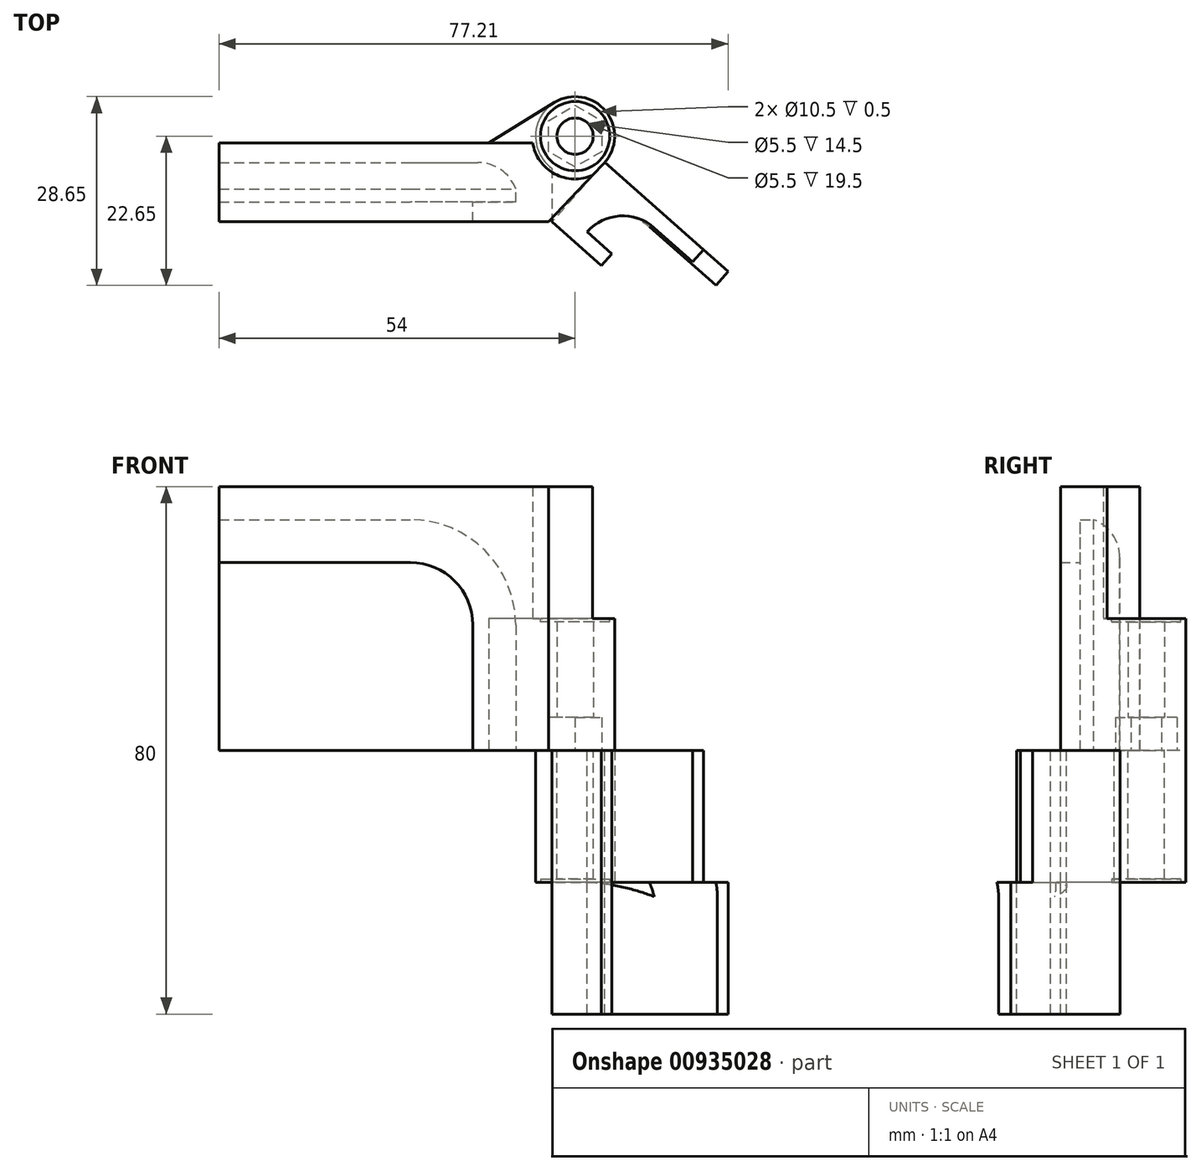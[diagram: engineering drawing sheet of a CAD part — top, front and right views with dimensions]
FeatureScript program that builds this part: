
annotation { "Feature Type Name" : "Feature", "Feature Type Description" : "" }
export const myFeature = defineFeature(function(context is Context, id is Id, definition is map)
    precondition{}
    {
        {
            var Q0;
            Q0=qCreatedBy(makeId("Front.planeOp"),FACE);
            var sketch = newSketch(context, id + "F0", { "sketchPlane" : qUnion([Q0])});
            skLineSegment(sketch, "E0.bottom", {"start": v(0, 0) * mm, "end": v(45, 0) * mm});
            skLineSegment(sketch, "E0.top", {"start": v(0, 35) * mm, "end": v(29, 35) * mm});
            skLineSegment(sketch, "E0.left", {"start": v(0, 0) * mm, "end": v(0, 35) * mm});
            skLineSegment(sketch, "E0.right", {"start": v(45, 0) * mm, "end": v(45, 19) * mm});
            skLineSegment(sketch, "E1.bottom", {"start": v(0, 0) * mm, "end": v(50, 0) * mm});
            skLineSegment(sketch, "E1.top", {"start": v(0, 40) * mm, "end": v(50, 40) * mm});
            skLineSegment(sketch, "E1.left", {"start": v(0, 0) * mm, "end": v(0, 40) * mm});
            skLineSegment(sketch, "E1.right", {"start": v(50, 0) * mm, "end": v(50, 40) * mm});
            skPoint(sketch, "E2.visualSharp", {"position": v(45, 35) * mm});
            skArc(sketch, "E2.filletArc", {"start": v(45, 19) * mm, "mid": v(40.31, 30.31) * mm, "end": v(29, 35) * mm});
            skSolve(sketch);
        }
        {
            var Q0;
            {var subQ4=sQuery(id+"F0.wireOp",EDGE,"E0.top");Q0=makeQuery(id+"F0.imprint","IMPRINT",FACE,{"disambiguationData":[TD([[makeQuery(id+"F0.imprint","IMPRINT",EDGE,{"derivedFrom":subQ4}),1.0]])]});}
            extrude(context, id + "F1", {"entities" : qUnion([Q0]), "depth" : 6 * mm, "offsetDistance" : 25 * mm});
        }
        {
            var Q0;
            {var subQ4=sQuery(id+"F0.wireOp",EDGE,"E0.top");Q0=makeQuery(id+"F0.imprint","IMPRINT",FACE,{"disambiguationData":[TD([[makeQuery(id+"F0.imprint","IMPRINT",EDGE,{"derivedFrom":subQ4}),-1.0]])]});}
            var Q1;
            {var subQ4=sQuery(id+"F0.wireOp",EDGE,"E0.top");Q1=makeQuery(id+"F0.imprint","IMPRINT",FACE,{"disambiguationData":[TD([[makeQuery(id+"F0.imprint","IMPRINT",EDGE,{"derivedFrom":subQ4}),1.0]])]});}
            extrude(context, id + "F2", {"entities" : qUnion([Q0, Q1]), "operationType" : NewBodyOperationType.ADD, "oppositeDirection" : true, "depth" : 3 * mm, "offsetDistance" : 25 * mm});
        }
        {
            var Q0;
            Q0=qCreatedBy(makeId("Right.planeOp"),FACE);
            var sketch = newSketch(context, id + "F3", { "sketchPlane" : qUnion([Q0])});
            skArc(sketch, "E3", {"start": v(0, 29.25) * mm, "mid": v(-1.1, 32.76) * mm, "end": v(-4.01, 35) * mm});
            skPoint(sketch, "E4.orphan", {"position": v(0, 35) * mm});
            skLineSegment(sketch, "E5", {"start": v(0, 29.25) * mm, "end": v(0, 35) * mm});
            skLineSegment(sketch, "E6", {"start": v(0, 35) * mm, "end": v(-4.01, 35) * mm});
            skPoint(sketch, "E7.0.start.orphan", {"position": v(-6, 35) * mm});
            skSolve(sketch);
        }
        {
            var Q0;
            Q0 = qSketchRegion(id + "F3", true);
            var Q1;
            Q1=sQuery(id+"F0.wireOp",EDGE,"E0.top");
            var Q2;
            Q2=sQuery(id+"F0.wireOp",EDGE,"E2.filletArc");
            var Q3;
            Q3=sQuery(id+"F0.wireOp",EDGE,"E0.right");
            sweep(context, id + "F4", {"operationType" : NewBodyOperationType.ADD, "profiles" : qUnion([Q0]), "path" : qUnion([Q1, Q2, Q3])});
        }
        {
            var Q0;
            Q0=makeQuery(id+"F1.opExtrude","CAP_FACE",FACE,{"disambiguationData":[OSD([sQuery(id+"F0.wireOp",EDGE,"E0.top"),sQuery(id+"F0.wireOp",EDGE,"E0.right"),sQuery(id+"F0.wireOp",EDGE,"E1.bottom"),sQuery(id+"F0.wireOp",EDGE,"E1.top"),sQuery(id+"F0.wireOp",EDGE,"E1.left"),sQuery(id+"F0.wireOp",EDGE,"E1.right"),sQuery(id+"F0.wireOp",EDGE,"E2.filletArc")])],"isStart":false});
            var sketch = newSketch(context, id + "F5", { "sketchPlane" : qUnion([Q0])});
            skLineSegment(sketch, "E8.0", {"start": v(0, 40) * mm, "end": v(50, 40) * mm});
            skLineSegment(sketch, "E9.0", {"start": v(50, 0) * mm, "end": v(50, 40) * mm});
            skLineSegment(sketch, "E10", {"start": v(0, 40) * mm, "end": v(0, 33.5) * mm});
            skLineSegment(sketch, "E11.0", {"start": v(43.5, 0) * mm, "end": v(43.5, 19) * mm});
            skArc(sketch, "E11.1", {"start": v(43.5, 19) * mm, "mid": v(39.25, 29.25) * mm, "end": v(29, 33.5) * mm});
            skLineSegment(sketch, "E11.2", {"start": v(0, 33.5) * mm, "end": v(29, 33.5) * mm});
            skLineSegment(sketch, "E12", {"start": v(43.5, 0) * mm, "end": v(50, 0) * mm});
            skLineSegment(sketch, "E13.0", {"start": v(38.5, 0) * mm, "end": v(38.5, 19) * mm});
            skArc(sketch, "E13.1", {"start": v(38.5, 19) * mm, "mid": v(35.72, 25.72) * mm, "end": v(29, 28.5) * mm});
            skLineSegment(sketch, "E13.2", {"start": v(0, 28.5) * mm, "end": v(29, 28.5) * mm});
            skLineSegment(sketch, "E14", {"start": v(0, 33.5) * mm, "end": v(0, 28.5) * mm});
            skLineSegment(sketch, "E15", {"start": v(38.5, 0) * mm, "end": v(43.5, 0) * mm});
            skLineSegment(sketch, "E16", {"start": v(29, 33.5) * mm, "end": v(29, 28.5) * mm});
            skLineSegment(sketch, "E17", {"start": v(43.5, 19) * mm, "end": v(38.5, 19) * mm});
            skSolve(sketch);
        }
        {
            var Q0;
            {var subQ5=sQuery(id+"F5.wireOp",EDGE,"E8.0");Q0=makeQuery(id+"F5.imprint","IMPRINT",FACE,{"disambiguationData":[TD([[makeQuery(id+"F5.imprint","IMPRINT",EDGE,{"derivedFrom":subQ5}),-1.0]])]});}
            var Q1;
            {var subQ1=sQuery(id+"F5.wireOp",EDGE,"E11.0");Q1=makeQuery(id+"F5.imprint","IMPRINT",FACE,{"disambiguationData":[TD([[makeQuery(id+"F5.imprint","IMPRINT",EDGE,{"derivedFrom":subQ1}),-1.0]])]});}
            var Q2;
            Q2=makeQuery(id+"F5.imprint","IMPRINT",FACE,{"disambiguationData":[TD([[makeQuery(id+"F5.imprint","IMPRINT",EDGE,{"derivedFrom":sQuery(id+"F5.wireOp",EDGE,"E11.0")}),1.0]])]});
            var Q3;
            Q3=makeQuery(id+"F5.imprint","IMPRINT",FACE,{"disambiguationData":[TD([[makeQuery(id+"F5.imprint","IMPRINT",EDGE,{"derivedFrom":sQuery(id+"F5.wireOp",EDGE,"E11.2")}),-1.0]])]});
            var Q4;
            Q4=makeQuery(id+"F5.imprint","IMPRINT",FACE,{"disambiguationData":[TD([[makeQuery(id+"F5.imprint","IMPRINT",EDGE,{"derivedFrom":sQuery(id+"F5.wireOp",EDGE,"E11.1")}),1.0]])]});
            extrude(context, id + "F6", {"entities" : qUnion([Q0, Q1, Q2, Q3, Q4]), "operationType" : NewBodyOperationType.ADD, "depth" : 3 * mm, "offsetDistance" : 25 * mm});
        }
        {
            var Q0;
            Q0=qCreatedBy(makeId("Top.planeOp"),FACE);
            var sketch = newSketch(context, id + "F7", { "sketchPlane" : qUnion([Q0])});
            skCircle(sketch, "E18", {"center": v(54, 4) * mm, "radius": 6 * mm});
            skCircle(sketch, "E19", {"center": v(54, 4) * mm, "radius": 2.75 * mm});
            skCircle(sketch, "E20.cCircle", {"center": v(54, 4) * mm, "radius": 4.68 * mm, "construction": true});
            skLineSegment(sketch, "E20.0", {"start": v(58.05, 6.34) * mm, "end": v(58.05, 1.66) * mm});
            skLineSegment(sketch, "E20.1", {"start": v(58.05, 1.66) * mm, "end": v(54, -0.68) * mm});
            skLineSegment(sketch, "E20.2", {"start": v(54, -0.68) * mm, "end": v(49.95, 1.66) * mm});
            skLineSegment(sketch, "E20.3", {"start": v(49.95, 1.66) * mm, "end": v(49.95, 6.34) * mm});
            skLineSegment(sketch, "E20.4", {"start": v(49.95, 6.34) * mm, "end": v(54, 8.68) * mm});
            skLineSegment(sketch, "E20.5", {"start": v(54, 8.68) * mm, "end": v(58.05, 6.34) * mm});
            skLineSegment(sketch, "E21", {"start": v(58.37, -0.11) * mm, "end": v(50, -9) * mm});
            skPoint(sketch, "E22.0", {"position": v(50, -9) * mm});
            skPoint(sketch, "E23.0", {"position": v(50, 3) * mm});
            skLineSegment(sketch, "E24", {"start": v(50.87, 9.12) * mm, "end": v(40.87, 3) * mm});
            skLineSegment(sketch, "E25", {"start": v(40.87, 3) * mm, "end": v(48.08, 3) * mm});
            skLineSegment(sketch, "E26", {"start": v(50, -9) * mm, "end": v(50, -0.47) * mm});
            skSolve(sketch);
        }
        {
            var Q0;
            {var subQ0=sQuery(id+"F7.wireOp",EDGE,"8cb6e2d6-110c-4912-a526-4a30d62b72c0");Q0=makeQuery(id+"F7.imprint","IMPRINT",FACE,{"disambiguationData":[TD([[makeQuery(id+"F7.imprint","IMPRINT",EDGE,{"derivedFrom":subQ0}),1.0]])]});}
            var Q1;
            Q1=makeQuery(id+"F7.imprint","IMPRINT",FACE,{"disambiguationData":[TD([[makeQuery(id+"F7.imprint","IMPRINT",EDGE,{"derivedFrom":sQuery(id+"F7.wireOp",EDGE,"E20.0")}),1.0]])]});
            var Q2;
            {var subQ0=sQuery(id+"F7.wireOp",EDGE,"0a3eac35-8b06-4a45-9f79-940ba3505365");Q2=makeQuery(id+"F7.imprint","IMPRINT",FACE,{"disambiguationData":[TD([[makeQuery(id+"F7.imprint","IMPRINT",EDGE,{"derivedFrom":subQ0}),-1.0]])]});}
            var Q3;
            {var subQ0=sQuery(id+"F7.wireOp",EDGE,"E24");Q3=makeQuery(id+"F7.imprint","IMPRINT",FACE,{"disambiguationData":[TD([[makeQuery(id+"F7.imprint","IMPRINT",EDGE,{"derivedFrom":subQ0}),1.0]])]});}
            var Q4;
            {var subQ0=sQuery(id+"F7.wireOp",EDGE,"E21");Q4=makeQuery(id+"F7.imprint","IMPRINT",FACE,{"disambiguationData":[TD([[makeQuery(id+"F7.imprint","IMPRINT",EDGE,{"derivedFrom":subQ0}),-1.0]])]});}
            extrude(context, id + "F8", {"entities" : qUnion([Q0, Q1, Q2, Q3, Q4]), "operationType" : NewBodyOperationType.ADD, "depth" : 5 * mm, "offsetDistance" : 25 * mm});
        }
        {
            var Q0;
            Q0=makeQuery(id+"F7.imprint","IMPRINT",FACE,{"disambiguationData":[TD([[makeQuery(id+"F7.imprint","IMPRINT",EDGE,{"derivedFrom":sQuery(id+"F7.wireOp",EDGE,"E19")}),-1.0]])]});
            extrude(context, id + "F9", {"entities" : qUnion([Q0]), "operationType" : NewBodyOperationType.REMOVE, "depth" : 5 * mm, "offsetDistance" : 25 * mm});
        }
        {
            var Q0;
            Q0=makeQuery(id+"F8.opExtrude","CAP_FACE",FACE,{"disambiguationData":[OSD([sQuery(id+"F7.wireOp",EDGE,"E18"),sQuery(id+"F7.wireOp",EDGE,"8cb6e2d6-110c-4912-a526-4a30d62b72c0"),sQuery(id+"F7.wireOp",EDGE,"0a3eac35-8b06-4a45-9f79-940ba3505365"),sQuery(id+"F7.wireOp",EDGE,"E20.0"),sQuery(id+"F7.wireOp",EDGE,"E20.1"),sQuery(id+"F7.wireOp",EDGE,"E20.2"),sQuery(id+"F7.wireOp",EDGE,"E20.3"),sQuery(id+"F7.wireOp",EDGE,"E20.4"),sQuery(id+"F7.wireOp",EDGE,"E20.5"),sQuery(id+"F7.wireOp",EDGE,"4abc8ff2-313a-444c-833f-485fd2e250e1.0")])],"isStart":false});
            var sketch = newSketch(context, id + "F10", { "sketchPlane" : qUnion([Q0])});
            skCircle(sketch, "E27.0", {"center": v(54, 4) * mm, "radius": 2.75 * mm});
            skCircle(sketch, "E28.0", {"center": v(54, 4) * mm, "radius": 6 * mm});
            skLineSegment(sketch, "E29.0", {"start": v(58.37, -0.11) * mm, "end": v(50, -9) * mm});
            skLineSegment(sketch, "E30.0", {"start": v(50, -9) * mm, "end": v(50, -0.47) * mm});
            skArc(sketch, "E31.0.0", {"start": v(58.37, -0.11) * mm, "mid": v(58.66, 7.78) * mm, "end": v(50.87, 9.12) * mm});
            skArc(sketch, "E31.0.1", {"start": v(50.87, 9.12) * mm, "mid": v(48.54, 6.49) * mm, "end": v(48.08, 3) * mm});
            skArc(sketch, "E31.0.2", {"start": v(48.08, 3) * mm, "mid": v(48.75, 1.1) * mm, "end": v(50, -0.47) * mm});
            skArc(sketch, "E31.0.3", {"start": v(50, -0.47) * mm, "mid": v(54.26, -2) * mm, "end": v(58.37, -0.11) * mm});
            skArc(sketch, "E32.0.0", {"start": v(48.08, 3) * mm, "mid": v(48.54, 6.49) * mm, "end": v(50.87, 9.12) * mm});
            skLineSegment(sketch, "E32.0.1", {"start": v(50.87, 9.12) * mm, "end": v(40.87, 3) * mm});
            skLineSegment(sketch, "E32.0.2", {"start": v(40.87, 3) * mm, "end": v(48.08, 3) * mm});
            skArc(sketch, "E33.0.0", {"start": v(58.37, -0.11) * mm, "mid": v(54.26, -2) * mm, "end": v(50, -0.47) * mm});
            skLineSegment(sketch, "E33.0.1", {"start": v(50, -0.47) * mm, "end": v(50, -9) * mm});
            skLineSegment(sketch, "E33.0.2", {"start": v(50, -9) * mm, "end": v(58.37, -0.11) * mm});
            skSolve(sketch);
        }
        {
            var Q0;
            {var subQ2=sQuery(id+"F10.wireOp",EDGE,"E33.0.1");Q0=makeQuery(id+"F10.imprint","IMPRINT",FACE,{"disambiguationData":[TD([[makeQuery(id+"F10.imprint","IMPRINT",EDGE,{"derivedFrom":subQ2}),-1.0]])]});}
            var Q1;
            {var subQ8=sQuery(id+"F7.wireOp",EDGE,"E20.0");Q1=makeQuery(id+"F10.imprint","IMPRINT",FACE,{"disambiguationData":[TD([[makeQuery(id+"F10.imprint","IMPRINT",EDGE,{"derivedFrom":makeQuery(id+"F8.opExtrude","CAP_EDGE",EDGE,{"disambiguationData":[OSD([subQ8])],"isStart":false})}),1.0]])]});}
            var Q2;
            Q2=makeQuery(id+"F10.imprint","IMPRINT",FACE,{"disambiguationData":[TD([[makeQuery(id+"F10.imprint","IMPRINT",EDGE,{"derivedFrom":sQuery(id+"F10.wireOp",EDGE,"E27.0")}),-1.0]])]});
            var Q3;
            {var subQ0=sQuery(id+"F10.wireOp",EDGE,"E32.0.1");Q3=makeQuery(id+"F10.imprint","IMPRINT",FACE,{"disambiguationData":[TD([[makeQuery(id+"F10.imprint","IMPRINT",EDGE,{"derivedFrom":subQ0}),1.0]])]});}
            extrude(context, id + "F11", {"entities" : qUnion([Q0, Q1, Q2, Q3]), "operationType" : NewBodyOperationType.ADD, "depth" : 15 * mm, "offsetDistance" : 25 * mm});
        }
        {
            var Q0;
            Q0=makeQuery(id+"F11.opExtrude","CAP_FACE",FACE,{"disambiguationData":[OSD([sQuery(id+"F10.wireOp",EDGE,"E27.0"),sQuery(id+"F10.wireOp",EDGE,"E28.0"),sQuery(id+"F10.wireOp",EDGE,"E33.0.1"),sQuery(id+"F10.wireOp",EDGE,"E33.0.2"),sQuery(id+"F10.wireOp",EDGE,"E32.0.1"),sQuery(id+"F10.wireOp",EDGE,"E32.0.2")])],"isStart":false});
            var sketch = newSketch(context, id + "F12", { "sketchPlane" : qUnion([Q0])});
            skCircle(sketch, "E34.0", {"center": v(54, 4) * mm, "radius": 6 * mm});
            skCircle(sketch, "E35.0", {"center": v(54, 4) * mm, "radius": 6.5 * mm});
            skSolve(sketch);
        }
        {
            var Q0;
            Q0 = qSketchRegion(id + "F12", true);
            var Q1;
            {var subQ0=sQuery(id+"F10.wireOp",EDGE,"E27.0");Q1=makeQuery(id+"F12.imprint","IMPRINT",FACE,{"disambiguationData":[TD([[makeQuery(id+"F12.imprint","IMPRINT",EDGE,{"derivedFrom":makeQuery(id+"F11.opExtrude","CAP_EDGE",EDGE,{"disambiguationData":[OSD([subQ0])],"isStart":false})}),-1.0]])]});}
            var Q2;
            {var subQ0=sQuery(id+"F12.wireOp",EDGE,"E34.0");var subQ1=makeQuery(id+"F11.opExtrude","CAP_FACE",FACE,{"disambiguationData":[OSD([sQuery(id+"F10.wireOp",EDGE,"E27.0"),sQuery(id+"F10.wireOp",EDGE,"E28.0"),sQuery(id+"F10.wireOp",EDGE,"E33.0.1"),sQuery(id+"F10.wireOp",EDGE,"E33.0.2"),sQuery(id+"F10.wireOp",EDGE,"E32.0.1"),sQuery(id+"F10.wireOp",EDGE,"E32.0.2")])],"isStart":false});var subQ2=sQuery(id+"F0.wireOp",EDGE,"E1.right");var subQ5=makeQuery(id+"F11.boolean.opBoolean","INTERSECT",EDGE,{"derivedFrom":[makeQuery(id+"F6.boolean.opBoolean","MERGE",FACE,{"derivedFrom":[makeQuery(id+"F2.boolean.opBoolean","MERGE",FACE,{"derivedFrom":[makeQuery(id+"F1.opExtrude","SWEPT_FACE",FACE,{"disambiguationData":[OSD([subQ2])]}),makeQuery(id+"F2.opExtrude","SWEPT_FACE",FACE,{"disambiguationData":[OSD([subQ2])]})]}),makeQuery(id+"F6.opExtrude","SWEPT_FACE",FACE,{"disambiguationData":[OSD([sQuery(id+"F5.wireOp",EDGE,"E9.0")])]})]}),subQ1]});var subQ6=makeQuery(id+"F12.imprint","INTERSECT",VERTEX,{"derivedFrom":[subQ5,subQ0]});Q2=makeQuery(id+"F12.imprint","IMPRINT",FACE,{"disambiguationData":[TD([[makeQuery(id+"F12.imprint","IMPRINT",EDGE,{"disambiguationData":[TD([[subQ6,1.0]])],"derivedFrom":subQ0}),1.0]])]});}
            extrude(context, id + "F13", {"entities" : qUnion([Q0, Q1, Q2]), "operationType" : NewBodyOperationType.REMOVE, "depth" : 25 * mm, "offsetDistance" : 25 * mm});
        }
        {
            var Q0;
            {var subQ0=sQuery(id+"F10.wireOp",EDGE,"E27.0");Q0=makeQuery(id+"F12.imprint","IMPRINT",FACE,{"disambiguationData":[TD([[makeQuery(id+"F12.imprint","IMPRINT",EDGE,{"derivedFrom":makeQuery(id+"F11.opExtrude","CAP_EDGE",EDGE,{"disambiguationData":[OSD([subQ0])],"isStart":false})}),-1.0]])]});}
            var sketch = newSketch(context, id + "F14", { "sketchPlane" : qUnion([Q0])});
            skCircle(sketch, "E36", {"center": v(54, 4) * mm, "radius": 5.25 * mm});
            skSolve(sketch);
        }
        {
            var Q0;
            {var subQ1=sQuery(id+"F10.wireOp",EDGE,"E27.0");Q0=makeQuery(id+"F14.imprint","IMPRINT",FACE,{"disambiguationData":[TD([[makeQuery(id+"F14.imprint","IMPRINT",EDGE,{"derivedFrom":makeQuery(id+"F12.imprint","IMPRINT",EDGE,{"derivedFrom":makeQuery(id+"F11.opExtrude","CAP_EDGE",EDGE,{"disambiguationData":[OSD([subQ1])],"isStart":false})})}),-1.0]])]});}
            var Q1;
            {var subQ0=sQuery(id+"F14.wireOp",EDGE,"E36");var subQ1=makeQuery(id+"F11.opExtrude","CAP_FACE",FACE,{"disambiguationData":[OSD([sQuery(id+"F10.wireOp",EDGE,"E27.0"),sQuery(id+"F10.wireOp",EDGE,"E28.0"),sQuery(id+"F10.wireOp",EDGE,"E33.0.1"),sQuery(id+"F10.wireOp",EDGE,"E33.0.2"),sQuery(id+"F10.wireOp",EDGE,"E32.0.1"),sQuery(id+"F10.wireOp",EDGE,"E32.0.2")])],"isStart":false});var subQ2=sQuery(id+"F0.wireOp",EDGE,"E1.right");var subQ4=makeQuery(id+"F11.boolean.opBoolean","INTERSECT",EDGE,{"derivedFrom":[makeQuery(id+"F6.boolean.opBoolean","MERGE",FACE,{"derivedFrom":[makeQuery(id+"F2.boolean.opBoolean","MERGE",FACE,{"derivedFrom":[makeQuery(id+"F1.opExtrude","SWEPT_FACE",FACE,{"disambiguationData":[OSD([subQ2])]}),makeQuery(id+"F2.opExtrude","SWEPT_FACE",FACE,{"disambiguationData":[OSD([subQ2])]})]}),makeQuery(id+"F6.opExtrude","SWEPT_FACE",FACE,{"disambiguationData":[OSD([sQuery(id+"F5.wireOp",EDGE,"E9.0")])]})]}),subQ1]});var subQ6=sQuery(id+"F12.wireOp",EDGE,"E34.0");var subQ7=makeQuery(id+"F12.imprint","IMPRINT",EDGE,{"disambiguationData":[TD([[makeQuery(id+"F12.imprint","INTERSECT",VERTEX,{"derivedFrom":[subQ4,subQ6]}),-1.0]])],"derivedFrom":subQ4});var subQ8=makeQuery(id+"F14.imprint","INTERSECT",VERTEX,{"derivedFrom":[subQ7,subQ0]});Q1=makeQuery(id+"F14.imprint","IMPRINT",FACE,{"disambiguationData":[TD([[makeQuery(id+"F14.imprint","IMPRINT",EDGE,{"disambiguationData":[TD([[subQ8,1.0]])],"derivedFrom":subQ0}),1.0]])]});}
            extrude(context, id + "F15", {"entities" : qUnion([Q0, Q1]), "operationType" : NewBodyOperationType.REMOVE, "oppositeDirection" : true, "depth" : 0.5 * mm, "offsetDistance" : 25 * mm});
        }
        {
            var Q0;
            {var subQ0=sQuery(id+"F0.wireOp",EDGE,"E1.bottom");Q0=makeQuery(id+"F8.boolean.opBoolean","MERGE",FACE,{"derivedFrom":[makeQuery(id+"F6.boolean.opBoolean","MERGE",FACE,{"derivedFrom":[makeQuery(id+"F4.boolean.opBoolean","MERGE",FACE,{"derivedFrom":[makeQuery(id+"F2.boolean.opBoolean","MERGE",FACE,{"derivedFrom":[makeQuery(id+"F1.opExtrude","SWEPT_FACE",FACE,{"disambiguationData":[OSD([subQ0])]}),makeQuery(id+"F2.opExtrude","SWEPT_FACE",FACE,{"disambiguationData":[OSD([subQ0])]})]}),makeQuery(id+"F4.opSweep","CAP_FACE",FACE,{"disambiguationData":[OSD([sQuery(id+"F0.wireOp",VERTEX,"E0.right.start"),sQuery(id+"F3.wireOp",EDGE,"E3"),sQuery(id+"F3.wireOp",EDGE,"E5"),sQuery(id+"F3.wireOp",EDGE,"E6")])],"isStart":false})]}),makeQuery(id+"F6.opExtrude","SWEPT_FACE",FACE,{"disambiguationData":[OSD([sQuery(id+"F5.wireOp",EDGE,"E12"),sQuery(id+"F5.wireOp",EDGE,"E15")])]})]}),makeQuery(id+"F8.opExtrude","CAP_FACE",FACE,{"disambiguationData":[OSD([sQuery(id+"F7.wireOp",EDGE,"E18"),sQuery(id+"F7.wireOp",EDGE,"8cb6e2d6-110c-4912-a526-4a30d62b72c0"),sQuery(id+"F7.wireOp",EDGE,"0a3eac35-8b06-4a45-9f79-940ba3505365"),sQuery(id+"F7.wireOp",EDGE,"E20.0"),sQuery(id+"F7.wireOp",EDGE,"E20.1"),sQuery(id+"F7.wireOp",EDGE,"E20.2"),sQuery(id+"F7.wireOp",EDGE,"E20.3"),sQuery(id+"F7.wireOp",EDGE,"E20.4"),sQuery(id+"F7.wireOp",EDGE,"E20.5"),sQuery(id+"F7.wireOp",EDGE,"4abc8ff2-313a-444c-833f-485fd2e250e1.0")])],"isStart":true})]});}
            var sketch = newSketch(context, id + "F16", { "sketchPlane" : qUnion([Q0])});
            skLineSegment(sketch, "E37.0.0", {"start": v(58.37, 0.11) * mm, "end": v(50, 9) * mm});
            skLineSegment(sketch, "E37.0.1", {"start": v(50, 9) * mm, "end": v(38.5, 9) * mm});
            skLineSegment(sketch, "E37.0.2", {"start": v(38.5, 9) * mm, "end": v(38.5, 6) * mm});
            skLineSegment(sketch, "E37.0.3", {"start": v(38.5, 6) * mm, "end": v(45, 6) * mm});
            skLineSegment(sketch, "E37.0.4", {"start": v(45, 6) * mm, "end": v(45, 4.01) * mm});
            skArc(sketch, "E37.0.5", {"start": v(45, 4.01) * mm, "mid": v(42.76, 1.1) * mm, "end": v(39.25, 0) * mm});
            skLineSegment(sketch, "E37.0.6", {"start": v(39.25, 0) * mm, "end": v(0, 0) * mm});
            skLineSegment(sketch, "E37.0.7", {"start": v(0, 0) * mm, "end": v(0, -3) * mm});
            skLineSegment(sketch, "E37.0.8", {"start": v(0, -3) * mm, "end": v(40.87, -3) * mm});
            skLineSegment(sketch, "E37.0.9", {"start": v(40.87, -3) * mm, "end": v(50.87, -9.12) * mm});
            skArc(sketch, "E37.0.10", {"start": v(50.87, -9.12) * mm, "mid": v(58.66, -7.78) * mm, "end": v(58.37, 0.11) * mm});
            skSolve(sketch);
        }
        {
            var Q0;
            Q0 = qSketchRegion(id + "F16", true);
            extrude(context, id + "F17", {"entities" : qUnion([Q0]), "oppositeDirection" : true, "depth" : 40 * mm, "offsetDistance" : 25 * mm});
        }
        {
            var Q0;
            Q0=makeQuery(id+"F7.imprint","IMPRINT",FACE,{"disambiguationData":[TD([[makeQuery(id+"F7.imprint","IMPRINT",EDGE,{"derivedFrom":sQuery(id+"F7.wireOp",EDGE,"E19")}),-1.0]])]});
            var Q1;
            Q1=makeQuery(id+"F7.imprint","IMPRINT",FACE,{"disambiguationData":[TD([[makeQuery(id+"F7.imprint","IMPRINT",EDGE,{"derivedFrom":sQuery(id+"F7.wireOp",EDGE,"E19")}),1.0]])]});
            extrude(context, id + "F18", {"entities" : qUnion([Q0, Q1]), "operationType" : NewBodyOperationType.REMOVE, "depth" : 5 * mm, "offsetDistance" : 25 * mm});
        }
        {
            var Q0;
            Q0=makeQuery(id+"F10.imprint","IMPRINT",FACE,{"disambiguationData":[TD([[makeQuery(id+"F10.imprint","IMPRINT",EDGE,{"derivedFrom":sQuery(id+"F10.wireOp",EDGE,"E27.0")}),1.0]])]});
            extrude(context, id + "F19", {"entities" : qUnion([Q0]), "operationType" : NewBodyOperationType.REMOVE, "endBound" : BoundingType.THROUGH_ALL, "depth" : 15 * mm, "offsetDistance" : 25 * mm});
        }
        {
            var Q0;
            Q0 = qSketchRegion(id + "F12", true);
            var Q1;
            {var subQ0=sQuery(id+"F12.wireOp",EDGE,"E35.0");var subQ1=sQuery(id+"F10.wireOp",EDGE,"E33.0.2");var subQ5=makeQuery(id+"F11.opExtrude","CAP_EDGE",EDGE,{"disambiguationData":[OSD([subQ1])],"isStart":false});var subQ6=makeQuery(id+"F12.imprint","INTERSECT",VERTEX,{"derivedFrom":[subQ5,subQ0]});Q1=makeQuery(id+"F12.imprint","IMPRINT",FACE,{"disambiguationData":[TD([[makeQuery(id+"F12.imprint","IMPRINT",EDGE,{"disambiguationData":[TD([[subQ6,1.0]])],"derivedFrom":subQ0}),-1.0]])]});}
            var Q2;
            {var subQ0=sQuery(id+"F12.wireOp",EDGE,"E35.0");var subQ1=sQuery(id+"F10.wireOp",EDGE,"E32.0.1");var subQ4=makeQuery(id+"F11.opExtrude","CAP_EDGE",EDGE,{"disambiguationData":[OSD([subQ1])],"isStart":false});var subQ5=makeQuery(id+"F12.imprint","INTERSECT",VERTEX,{"derivedFrom":[subQ4,subQ0]});Q2=makeQuery(id+"F12.imprint","IMPRINT",FACE,{"disambiguationData":[TD([[makeQuery(id+"F12.imprint","IMPRINT",EDGE,{"disambiguationData":[TD([[subQ5,-1.0]])],"derivedFrom":subQ0}),-1.0]])]});}
            var Q3;
            {var subQ0=sQuery(id+"F12.wireOp",EDGE,"E34.0");var subQ1=makeQuery(id+"F11.opExtrude","CAP_FACE",FACE,{"disambiguationData":[OSD([sQuery(id+"F10.wireOp",EDGE,"E27.0"),sQuery(id+"F10.wireOp",EDGE,"E28.0"),sQuery(id+"F10.wireOp",EDGE,"E33.0.1"),sQuery(id+"F10.wireOp",EDGE,"E33.0.2"),sQuery(id+"F10.wireOp",EDGE,"E32.0.1"),sQuery(id+"F10.wireOp",EDGE,"E32.0.2")])],"isStart":false});var subQ2=sQuery(id+"F0.wireOp",EDGE,"E1.right");var subQ5=makeQuery(id+"F11.boolean.opBoolean","INTERSECT",EDGE,{"derivedFrom":[makeQuery(id+"F6.boolean.opBoolean","MERGE",FACE,{"derivedFrom":[makeQuery(id+"F2.boolean.opBoolean","MERGE",FACE,{"derivedFrom":[makeQuery(id+"F1.opExtrude","SWEPT_FACE",FACE,{"disambiguationData":[OSD([subQ2])]}),makeQuery(id+"F2.opExtrude","SWEPT_FACE",FACE,{"disambiguationData":[OSD([subQ2])]})]}),makeQuery(id+"F6.opExtrude","SWEPT_FACE",FACE,{"disambiguationData":[OSD([sQuery(id+"F5.wireOp",EDGE,"E9.0")])]})]}),subQ1]});var subQ6=makeQuery(id+"F12.imprint","INTERSECT",VERTEX,{"derivedFrom":[subQ5,subQ0]});Q3=makeQuery(id+"F12.imprint","IMPRINT",FACE,{"disambiguationData":[TD([[makeQuery(id+"F12.imprint","IMPRINT",EDGE,{"disambiguationData":[TD([[subQ6,1.0]])],"derivedFrom":subQ0}),1.0]])]});}
            var Q4;
            {var subQ0=sQuery(id+"F10.wireOp",EDGE,"E27.0");Q4=makeQuery(id+"F12.imprint","IMPRINT",FACE,{"disambiguationData":[TD([[makeQuery(id+"F12.imprint","IMPRINT",EDGE,{"derivedFrom":makeQuery(id+"F11.opExtrude","CAP_EDGE",EDGE,{"disambiguationData":[OSD([subQ0])],"isStart":false})}),-1.0]])]});}
            var Q5;
            Q5=makeQuery(id+"F12.imprint","IMPRINT",FACE,{"disambiguationData":[TD([[makeQuery(id+"F12.imprint","IMPRINT",EDGE,{"derivedFrom":makeQuery(id+"F11.opExtrude","CAP_EDGE",EDGE,{"disambiguationData":[OSD([sQuery(id+"F10.wireOp",EDGE,"E27.0")])],"isStart":false})}),1.0]])]});
            extrude(context, id + "F20", {"entities" : qUnion([Q0, Q1, Q2, Q3, Q4, Q5]), "operationType" : NewBodyOperationType.REMOVE, "depth" : 25 * mm, "offsetDistance" : 25 * mm});
        }
        {
            var Q0;
            {var subQ0=sQuery(id+"F14.wireOp",EDGE,"E36");var subQ1=makeQuery(id+"F11.opExtrude","CAP_FACE",FACE,{"disambiguationData":[OSD([sQuery(id+"F10.wireOp",EDGE,"E27.0"),sQuery(id+"F10.wireOp",EDGE,"E28.0"),sQuery(id+"F10.wireOp",EDGE,"E33.0.1"),sQuery(id+"F10.wireOp",EDGE,"E33.0.2"),sQuery(id+"F10.wireOp",EDGE,"E32.0.1"),sQuery(id+"F10.wireOp",EDGE,"E32.0.2")])],"isStart":false});var subQ2=sQuery(id+"F0.wireOp",EDGE,"E1.right");var subQ4=makeQuery(id+"F11.boolean.opBoolean","INTERSECT",EDGE,{"derivedFrom":[makeQuery(id+"F6.boolean.opBoolean","MERGE",FACE,{"derivedFrom":[makeQuery(id+"F2.boolean.opBoolean","MERGE",FACE,{"derivedFrom":[makeQuery(id+"F1.opExtrude","SWEPT_FACE",FACE,{"disambiguationData":[OSD([subQ2])]}),makeQuery(id+"F2.opExtrude","SWEPT_FACE",FACE,{"disambiguationData":[OSD([subQ2])]})]}),makeQuery(id+"F6.opExtrude","SWEPT_FACE",FACE,{"disambiguationData":[OSD([sQuery(id+"F5.wireOp",EDGE,"E9.0")])]})]}),subQ1]});var subQ6=sQuery(id+"F12.wireOp",EDGE,"E34.0");var subQ7=makeQuery(id+"F12.imprint","IMPRINT",EDGE,{"disambiguationData":[TD([[makeQuery(id+"F12.imprint","INTERSECT",VERTEX,{"derivedFrom":[subQ4,subQ6]}),-1.0]])],"derivedFrom":subQ4});var subQ8=makeQuery(id+"F14.imprint","INTERSECT",VERTEX,{"derivedFrom":[subQ7,subQ0]});Q0=makeQuery(id+"F14.imprint","IMPRINT",FACE,{"disambiguationData":[TD([[makeQuery(id+"F14.imprint","IMPRINT",EDGE,{"disambiguationData":[TD([[subQ8,1.0]])],"derivedFrom":subQ0}),1.0]])]});}
            var Q1;
            {var subQ1=sQuery(id+"F10.wireOp",EDGE,"E27.0");Q1=makeQuery(id+"F14.imprint","IMPRINT",FACE,{"disambiguationData":[TD([[makeQuery(id+"F14.imprint","IMPRINT",EDGE,{"derivedFrom":makeQuery(id+"F12.imprint","IMPRINT",EDGE,{"derivedFrom":makeQuery(id+"F11.opExtrude","CAP_EDGE",EDGE,{"disambiguationData":[OSD([subQ1])],"isStart":false})})}),-1.0]])]});}
            extrude(context, id + "F21", {"entities" : qUnion([Q0, Q1]), "operationType" : NewBodyOperationType.REMOVE, "oppositeDirection" : true, "depth" : 0.5 * mm, "offsetDistance" : 25 * mm});
        }
        {
            var Q0;
            Q0=qCreatedBy(makeId("Top.planeOp"),FACE);
            var sketch = newSketch(context, id + "F22", { "sketchPlane" : qUnion([Q0])});
            skCircle(sketch, "E38.0", {"center": v(54, 4) * mm, "radius": 2.75 * mm});
            skArc(sketch, "E39.0", {"start": v(50.87, 9.12) * mm, "mid": v(48.54, 6.49) * mm, "end": v(48.08, 3) * mm});
            skArc(sketch, "E40.0", {"start": v(50, -0.47) * mm, "mid": v(54.26, -2) * mm, "end": v(58.37, -0.11) * mm});
            skArc(sketch, "E40.1", {"start": v(58.37, -0.11) * mm, "mid": v(58.66, 7.78) * mm, "end": v(50.87, 9.12) * mm});
            skArc(sketch, "E40.2", {"start": v(48.08, 3) * mm, "mid": v(48.75, 1.1) * mm, "end": v(50, -0.47) * mm});
            skCircle(sketch, "E41.0", {"center": v(54, 4) * mm, "radius": 5.25 * mm});
            skLineSegment(sketch, "E42", {"start": v(50.5, -0.87) * mm, "end": v(50.5, -9) * mm});
            skLineSegment(sketch, "E43", {"start": v(58.46, -0.02) * mm, "end": v(50.5, -9) * mm});
            skLineSegment(sketch, "E44", {"start": v(58.46, -0.02) * mm, "end": v(58.5, 0.02) * mm});
            skSolve(sketch);
        }
        {
            var Q0;
            Q0=makeQuery(id+"F22.imprint","IMPRINT",FACE,{"disambiguationData":[TD([[makeQuery(id+"F22.imprint","IMPRINT",EDGE,{"derivedFrom":sQuery(id+"F22.wireOp",EDGE,"E38.0")}),-1.0]])]});
            var Q1;
            {var subQ5=sQuery(id+"F22.wireOp",EDGE,"E44");Q1=makeQuery(id+"F22.imprint","IMPRINT",FACE,{"disambiguationData":[TD([[makeQuery(id+"F22.imprint","IMPRINT",EDGE,{"derivedFrom":subQ5}),1.0]])]});}
            var Q2;
            {var subQ6=sQuery(id+"F22.wireOp",EDGE,"E39.0");Q2=makeQuery(id+"F22.imprint","IMPRINT",FACE,{"disambiguationData":[TD([[makeQuery(id+"F22.imprint","IMPRINT",EDGE,{"derivedFrom":subQ6}),1.0]])]});}
            extrude(context, id + "F23", {"entities" : qUnion([Q0, Q1, Q2]), "oppositeDirection" : true, "depth" : 20 * mm, "offsetDistance" : 25 * mm});
        }
        {
            var Q0;
            Q0=makeQuery(id+"F23.opExtrude","CAP_FACE",FACE,{"disambiguationData":[OSD([sQuery(id+"F22.wireOp",EDGE,"E38.0"),sQuery(id+"F22.wireOp",EDGE,"E39.0"),sQuery(id+"F22.wireOp",EDGE,"E40.0"),sQuery(id+"F22.wireOp",EDGE,"E40.1"),sQuery(id+"F22.wireOp",EDGE,"E40.2"),sQuery(id+"F22.wireOp",EDGE,"E42"),sQuery(id+"F22.wireOp",EDGE,"E43"),sQuery(id+"F22.wireOp",EDGE,"E44")])],"isStart":false});
            var sketch = newSketch(context, id + "F24", { "sketchPlane" : qUnion([Q0])});
            skCircle(sketch, "E45.0", {"center": v(54, -4) * mm, "radius": 5.25 * mm});
            skSolve(sketch);
        }
        {
            var Q0;
            Q0=makeQuery(id+"F24.imprint","IMPRINT",FACE,{"disambiguationData":[TD([[makeQuery(id+"F24.imprint","IMPRINT",EDGE,{"derivedFrom":sQuery(id+"F24.wireOp",EDGE,"E45.0")}),1.0]])]});
            extrude(context, id + "F25", {"entities" : qUnion([Q0]), "operationType" : NewBodyOperationType.REMOVE, "oppositeDirection" : true, "depth" : 0.5 * mm, "offsetDistance" : 25 * mm});
        }
        {
            var Q0;
            Q0=makeQuery(id+"F23.opExtrude","SWEPT_FACE",FACE,{"disambiguationData":[OSD([sQuery(id+"F22.wireOp",EDGE,"E43")])]});
            var sketch = newSketch(context, id + "F26", { "sketchPlane" : qUnion([Q0])});
            skLineSegment(sketch, "E46.bottom", {"start": v(26.75, 0) * mm, "end": v(26.75, 0) * mm});
            skLineSegment(sketch, "E46.top", {"start": v(26.75, -40) * mm, "end": v(26.75, -40) * mm});
            skLineSegment(sketch, "E46.left", {"start": v(26.75, 0) * mm, "end": v(26.75, -40) * mm});
            skLineSegment(sketch, "E46.right", {"start": v(26.75, 0) * mm, "end": v(26.75, -40) * mm});
            skLineSegment(sketch, "E47", {"start": v(29.15, -40) * mm, "end": v(29.15, -15) * mm});
            skLineSegment(sketch, "E48", {"start": v(36.35, -22.2) * mm, "end": v(36.35, -40) * mm});
            skPoint(sketch, "E49.visualSharp", {"position": v(36.35, -15) * mm});
            skArc(sketch, "E49.filletArc", {"start": v(36.35, -22.2) * mm, "mid": v(34.24, -17.1) * mm, "end": v(29.15, -15) * mm});
            skLineSegment(sketch, "E50", {"start": v(26.75, -20) * mm, "end": v(29.15, -20) * mm});
            skLineSegment(sketch, "E51", {"start": v(29.15, -20) * mm, "end": v(26.75, -20) * mm});
            skLineSegment(sketch, "E52", {"start": v(36.35, -40) * mm, "end": v(38.8, -40) * mm});
            skLineSegment(sketch, "E53", {"start": v(38.8, -40) * mm, "end": v(38.8, 0) * mm});
            skLineSegment(sketch, "E54", {"start": v(38.8, 0) * mm, "end": v(26.75, 0) * mm});
            skSolve(sketch);
        }
        {
            var Q0;
            {var subQ5=sQuery(id+"F26.wireOp",EDGE,"E51");Q0=makeQuery(id+"F26.imprint","IMPRINT",FACE,{"disambiguationData":[TD([[makeQuery(id+"F26.imprint","IMPRINT",EDGE,{"derivedFrom":subQ5}),-1.0]])]});}
            var Q1;
            {var subQ2=sQuery(id+"F26.wireOp",EDGE,"E48");Q1=makeQuery(id+"F26.imprint","IMPRINT",FACE,{"disambiguationData":[TD([[makeQuery(id+"F26.imprint","IMPRINT",EDGE,{"derivedFrom":subQ2}),1.0]])]});}
            extrude(context, id + "F27", {"entities" : qUnion([Q0, Q1]), "operationType" : NewBodyOperationType.ADD, "depth" : 25 * mm, "offsetDistance" : 25 * mm});
        }
        {
            var Q0;
            Q0=makeQuery(id+"F27.boolean.opBoolean","MERGE",FACE,{"derivedFrom":[makeQuery(id+"F23.opExtrude","CAP_FACE",FACE,{"disambiguationData":[OSD([sQuery(id+"F22.wireOp",EDGE,"E38.0"),sQuery(id+"F22.wireOp",EDGE,"E39.0"),sQuery(id+"F22.wireOp",EDGE,"E40.0"),sQuery(id+"F22.wireOp",EDGE,"E40.1"),sQuery(id+"F22.wireOp",EDGE,"E40.2"),sQuery(id+"F22.wireOp",EDGE,"E42"),sQuery(id+"F22.wireOp",EDGE,"E43"),sQuery(id+"F22.wireOp",EDGE,"E44")])],"isStart":false}),makeQuery(id+"F27.opExtrude","SWEPT_FACE",FACE,{"disambiguationData":[OSD([sQuery(id+"F26.wireOp",EDGE,"E51")])]})]});
            var sketch = newSketch(context, id + "F28", { "sketchPlane" : qUnion([Q0])});
            skLineSegment(sketch, "E55", {"start": v(58.5, -0.02) * mm, "end": v(52.1, 7.2) * mm});
            skLineSegment(sketch, "E56", {"start": v(58.5, -0.02) * mm, "end": v(73.46, 13.24) * mm});
            skLineSegment(sketch, "E57", {"start": v(66, 9.9) * mm, "end": v(66, 9.9) * mm});
            skArc(sketch, "E58.filletArc", {"start": v(55.83, 10.52) * mm, "mid": v(60.79, 8.1) * mm, "end": v(66, 9.9) * mm});
            skLineSegment(sketch, "E59", {"start": v(52.1, 7.2) * mm, "end": v(50.5, 9) * mm});
            skLineSegment(sketch, "E60", {"start": v(50.5, 9) * mm, "end": v(57.99, 15.63) * mm});
            skLineSegment(sketch, "E61", {"start": v(57.99, 15.63) * mm, "end": v(59.58, 13.83) * mm});
            skLineSegment(sketch, "E62", {"start": v(59.58, 13.83) * mm, "end": v(55.83, 10.52) * mm});
            skLineSegment(sketch, "E63", {"start": v(55.83, 10.52) * mm, "end": v(55.83, 10.52) * mm});
            skLineSegment(sketch, "E64", {"start": v(66, 9.9) * mm, "end": v(71.84, 15.08) * mm});
            skLineSegment(sketch, "E65", {"start": v(71.84, 15.08) * mm, "end": v(73.46, 13.24) * mm});
            skSolve(sketch);
        }
        {
            var Q0;
            {var subQ1=sQuery(id+"F28.wireOp",EDGE,"E59");Q0=makeQuery(id+"F28.imprint","IMPRINT",FACE,{"disambiguationData":[TD([[makeQuery(id+"F28.imprint","IMPRINT",EDGE,{"derivedFrom":subQ1}),-1.0]])]});}
            var Q1;
            {var subQ1=sQuery(id+"F28.wireOp",EDGE,"E56");Q1=makeQuery(id+"F28.imprint","IMPRINT",FACE,{"disambiguationData":[TD([[makeQuery(id+"F28.imprint","IMPRINT",EDGE,{"derivedFrom":subQ1}),1.0]])]});}
            var Q2;
            Q2=makeQuery(id+"F27.opExtrude","SWEPT_FACE",FACE,{"disambiguationData":[OSD([sQuery(id+"F26.wireOp",EDGE,"E52")])]});
            var Q3;
            Q3=makeQuery(id+"F27.boolean.opBoolean","MERGE",FACE,{"derivedFrom":[makeQuery(id+"F23.opExtrude","CAP_FACE",FACE,{"disambiguationData":[OSD([sQuery(id+"F22.wireOp",EDGE,"E38.0"),sQuery(id+"F22.wireOp",EDGE,"E39.0"),sQuery(id+"F22.wireOp",EDGE,"E40.0"),sQuery(id+"F22.wireOp",EDGE,"E40.1"),sQuery(id+"F22.wireOp",EDGE,"E40.2"),sQuery(id+"F22.wireOp",EDGE,"E42"),sQuery(id+"F22.wireOp",EDGE,"E43"),sQuery(id+"F22.wireOp",EDGE,"E44")])],"isStart":true}),makeQuery(id+"F27.opExtrude","SWEPT_FACE",FACE,{"disambiguationData":[OSD([sQuery(id+"F26.wireOp",EDGE,"E54")])]})]});
            extrude(context, id + "F29", {"entities" : qUnion([Q0, Q1]), "operationType" : NewBodyOperationType.ADD, "endBound" : BoundingType.UP_TO_SURFACE, "depth" : 25 * mm, "endBoundEntityFace" : qUnion([Q2]), "offsetDistance" : 25 * mm, "hasSecondDirection" : true, "secondDirectionBound" : SecondDirectionBoundingType.UP_TO_SURFACE, "secondDirectionOppositeDirection" : true, "secondDirectionDepth" : 25 * mm, "secondDirectionBoundEntityFace" : qUnion([Q3])});
        }
        {
            var Q0;
            Q0=makeQuery(id+"F29.boolean.opBoolean","INTERSECT",EDGE,{"derivedFrom":[makeQuery(id+"F27.opExtrude","SWEPT_FACE",FACE,{"disambiguationData":[OSD([sQuery(id+"F26.wireOp",EDGE,"E49.filletArc")])]}),makeQuery(id+"F29.opExtrude","SWEPT_FACE",FACE,{"disambiguationData":[OSD([sQuery(id+"F28.wireOp",EDGE,"E58.filletArc")])]})]});
            var Q1;
            Q1=makeQuery(id+"F29.opExtrude","CAP_EDGE",EDGE,{"disambiguationData":[OSD([sQuery(id+"F28.wireOp",EDGE,"E63")])],"isStart":true});
            var Q2;
            Q2=makeQuery(id+"F29.boolean.opBoolean","INTERSECT",EDGE,{"derivedFrom":[makeQuery(id+"F27.boolean.opBoolean","MERGE",FACE,{"derivedFrom":[makeQuery(id+"F23.opExtrude","CAP_FACE",FACE,{"disambiguationData":[OSD([sQuery(id+"F22.wireOp",EDGE,"E38.0"),sQuery(id+"F22.wireOp",EDGE,"E39.0"),sQuery(id+"F22.wireOp",EDGE,"E40.0"),sQuery(id+"F22.wireOp",EDGE,"E40.1"),sQuery(id+"F22.wireOp",EDGE,"E40.2"),sQuery(id+"F22.wireOp",EDGE,"E42"),sQuery(id+"F22.wireOp",EDGE,"E43"),sQuery(id+"F22.wireOp",EDGE,"E44")])],"isStart":false}),makeQuery(id+"F27.opExtrude","SWEPT_FACE",FACE,{"disambiguationData":[OSD([sQuery(id+"F26.wireOp",EDGE,"E51")])]})]}),makeQuery(id+"F29.opExtrude","SWEPT_FACE",FACE,{"disambiguationData":[OSD([sQuery(id+"F28.wireOp",EDGE,"E61")])]})]});
            fillet(context, id + "F30", {"entities" : qUnion([Q0, Q1, Q2]), "radius" : 5 * mm, "tangentPropagation" : true, "allowEdgeOverflow" : false});
        }
    });
